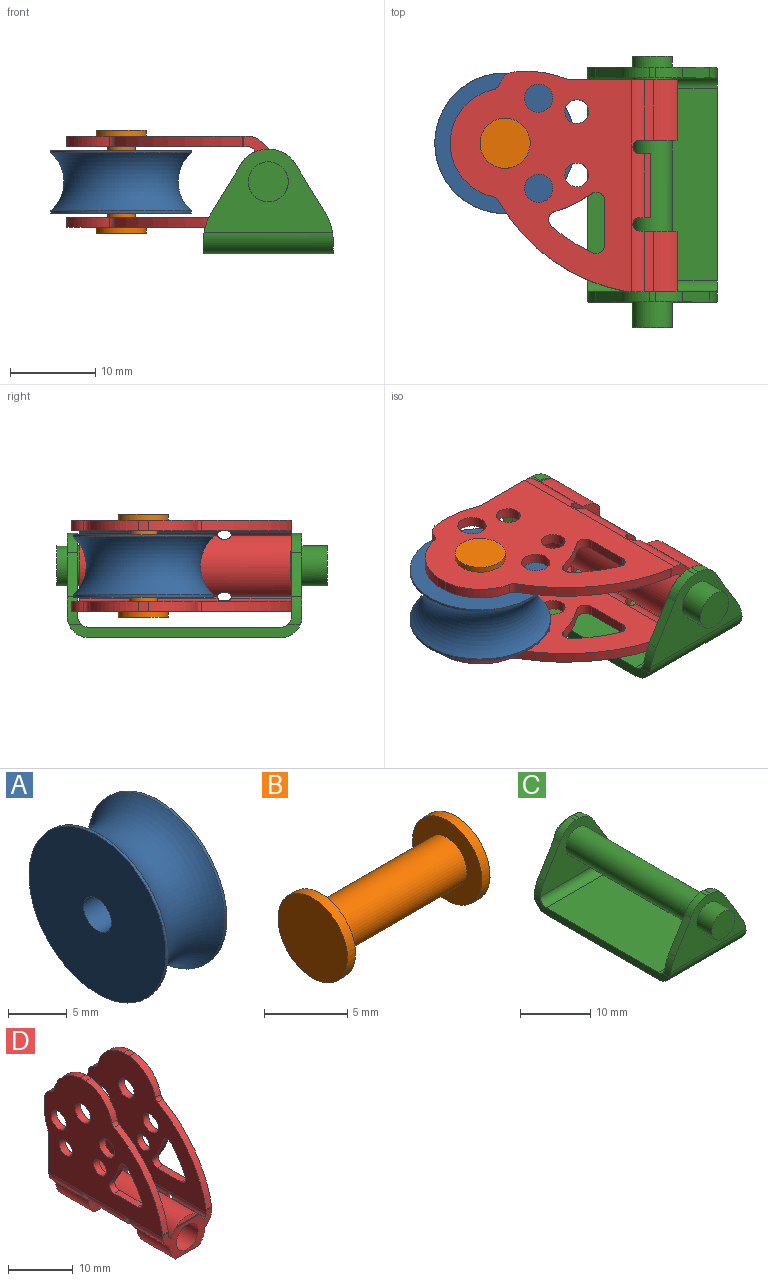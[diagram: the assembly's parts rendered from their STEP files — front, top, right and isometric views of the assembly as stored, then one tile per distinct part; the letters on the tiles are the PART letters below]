
ASSEMBLY  parts=4 mates=3
PART A: 6 faces, bbox 9x24.3x24.3 mm
  f0: cylinder r=8.26mm len=16.51mm, axis (-1,0,0), area 14.2mm2, adj f3,f5
  f1: cylinder r=8.26mm len=16.51mm, axis (-1,0,0), area 14.3mm2, adj f2,f5
  f2: plane 16.51x16.51mm, normal (1,0,0), area 205.3mm2, adj f1,f4
  f3: plane 16.51x16.51mm, normal (-1,0,0), area 205.3mm2, adj f0,f4
  f4: cylinder r=1.68mm len=7.35mm, axis (-1,0,0), area 77.5mm2, adj f2,f3
  f5: torus R=11.22mm, axis (-1,0,0), area 350.3mm2, adj f0,f1
PART B: 7 faces, bbox 12.1x5.9x5.9 mm
  f0: plane 5.89x5.89mm, normal (1,0,0), area 18.4mm2, adj f1,f3
  f1: cylinder r=2.95mm len=5.89mm, axis (1,0,0), area 12.7mm2, adj f0,f2
  f2: plane 5.89x5.89mm, normal (-1,0,0), area 27.3mm2, adj f1
  f3: cylinder r=1.68mm len=10.72mm, axis (1,0,0), area 112.9mm2, adj f0,f6
  f4: plane 5.89x5.89mm, normal (1,0,0), area 27.3mm2, adj f5
  f5: cylinder r=2.95mm len=5.89mm, axis (-1,0,0), area 12.7mm2, adj f4,f6
  f6: plane 5.89x5.89mm, normal (-1,0,0), area 18.4mm2, adj f3,f5
PART C: 31 faces, bbox 15.2x31.9x12.3 mm
  f0: cylinder r=2.35mm len=4.7mm, axis (0,1,0), area 44.2mm2, adj f1,f8
  f1: plane 4.7x4.7mm, normal (0,-1,0), area 17.3mm2, adj f0
  f2: plane 27.18x1.5mm, normal (1,0,0), area 32.2mm2, adj f3,f4,f5,f9,f10,f11,f24,f25
  f3: cylinder r=1.27mm len=15.24mm, axis (-1,0,0), area 30.4mm2, adj f2,f4,f12,f14,f20,f24
  f4: plane 22.61x15.24mm, normal (0,0,1), area 344.5mm2, adj f2,f3,f5,f12
  f5: cylinder r=1.27mm len=15.24mm, axis (-1,0,0), area 30.4mm2, adj f2,f4,f6,f12,f25,f29
  f6: plane 15.09x9.79mm, normal (0,1,0), area 80.7mm2, adj f5,f7,f16,f25,f26,f27,f28,f29
  f7: plane 1.22x0.65mm, normal (0,0,1), area 0.8mm2, adj f6,f8,f27,f30
  f8: plane 15.09x9.79mm, normal (0,-1,0), area 80.7mm2, adj f0,f7,f9,f25,f26,f27,f28,f29
  f9: cylinder r=2.49mm len=15.24mm, axis (-1,0,0), area 59.5mm2, adj f2,f8,f10,f12,f25,f29
  f10: plane 22.61x15.24mm, normal (0,0,-1), area 344.5mm2, adj f2,f9,f11,f12
  f11: cylinder r=2.49mm len=15.24mm, axis (-1,0,0), area 59.5mm2, adj f2,f10,f12,f13,f20,f24
  f12: plane 27.18x1.5mm, normal (-1,0,0), area 32.2mm2, adj f3,f4,f5,f9,f10,f11,f20,f29
  f13: plane 15.09x9.79mm, normal (0,1,0), area 80.7mm2, adj f11,f15,f18,f19,f20,f21,f22,f23
  f14: plane 15.09x9.79mm, normal (0,-1,0), area 80.7mm2, adj f3,f15,f16,f19,f20,f21,f22,f23
  f15: plane 1.22x0.65mm, normal (0,0,1), area 0.8mm2, adj f13,f14,f19,f22
  f16: cylinder r=2.35mm len=25.15mm, axis (0,1,0), area 371.2mm2, adj f6,f14
  f17: plane 4.7x4.7mm, normal (0,1,0), area 17.3mm2, adj f18
  f18: cylinder r=2.35mm len=4.7mm, axis (0,1,0), area 18.7mm2, adj f13,f17
  f19: cylinder r=3.85mm len=3.22mm, axis (0,1,0), area 5.1mm2, adj f13,f14,f15,f21
  f20: cylinder r=6.35mm len=3.32mm, axis (0,1,0), area 4.3mm2, adj f3,f11,f12,f13,f14,f21
  f21: plane 5.13x3.14mm, normal (-0.85,0,0.52), area 7.3mm2, adj f13,f14,f19,f20
  f22: cylinder r=3.85mm len=3.22mm, axis (0,1,0), area 5.1mm2, adj f13,f14,f15,f23
  f23: plane 5.13x3.14mm, normal (0.85,0,0.52), area 7.3mm2, adj f13,f14,f22,f24
  f24: cylinder r=6.35mm len=3.32mm, axis (0,1,0), area 4.3mm2, adj f2,f3,f11,f13,f14,f23
  f25: cylinder r=6.35mm len=3.32mm, axis (0,1,0), area 4.3mm2, adj f2,f5,f6,f8,f9,f26
  f26: plane 5.13x3.14mm, normal (0.85,0,0.52), area 7.3mm2, adj f6,f8,f25,f27
  f27: cylinder r=3.85mm len=3.22mm, axis (0,1,0), area 5.1mm2, adj f6,f7,f8,f26
  f28: plane 5.13x3.14mm, normal (-0.85,0,0.52), area 7.3mm2, adj f6,f8,f29,f30
  f29: cylinder r=6.35mm len=3.32mm, axis (0,1,0), area 4.3mm2, adj f5,f6,f8,f9,f12,f28
  f30: cylinder r=3.85mm len=3.22mm, axis (0,1,0), area 5.1mm2, adj f6,f7,f8,f28
PART D: 96 faces, bbox 10.7x25.9x26.6 mm
  f0: cylinder r=2.35mm len=24.89mm, axis (0,1,0), area 268.2mm2, adj f9,f12,f13,f14,f15,f16,f17,f18
  f1: cylinder r=6.45mm len=5.7mm, axis (-1,0,0), area 9.9mm2, adj f2,f51,f52,f72
  f2: cylinder r=1.02mm len=1.22mm, axis (-1,0,0), area 1.3mm2, adj f1,f3,f51,f52
  f3: cylinder r=2.03mm len=1.69mm, axis (-1,0,0), area 2.8mm2, adj f2,f4,f51,f52
  f4: cylinder r=12.7mm len=6.27mm, axis (-1,0,0), area 7.8mm2, adj f3,f11,f51,f52
  f5: cylinder r=6.45mm len=5.7mm, axis (-1,0,0), area 9.9mm2, adj f6,f41,f68,f73
  f6: cylinder r=1.02mm len=1.22mm, axis (-1,0,0), area 1.3mm2, adj f5,f7,f41,f68
  f7: cylinder r=2.03mm len=1.69mm, axis (-1,0,0), area 2.8mm2, adj f6,f8,f41,f68
  f8: cylinder r=12.7mm len=6.27mm, axis (-1,0,0), area 7.8mm2, adj f7,f10,f41,f68
  f9: plane 12.54x10.72mm, normal (0,1,0), area 48.6mm2, adj f0,f10,f11,f28,f41,f42,f47,f50
  f10: cylinder r=1.02mm len=1.22mm, axis (-1,0,0), area 0.5mm2, adj f8,f9,f41,f68
  f11: cylinder r=1.02mm len=1.22mm, axis (-1,0,0), area 0.5mm2, adj f4,f9,f51,f52
  f12: plane 10.3x4.41mm, normal (0,-1,0), area 18.6mm2, adj f0,f13,f14,f24,f26,f28,f42,f47
  f13: cylinder r=0.79mm len=3mm, axis (-1,0,0), area 5.3mm2, adj f0,f12,f15,f58,f59,f60
  f14: cylinder r=0.79mm len=3mm, axis (-1,0,0), area 5.3mm2, adj f0,f12,f16,f60,f62,f63
  f15: plane 3.33x1.26mm, normal (0,1,0), area 3.2mm2, adj f0,f13,f17,f26,f49,f50,f55,f58
  f16: plane 3.33x1.26mm, normal (0,1,0), area 3.2mm2, adj f0,f14,f18,f24,f42,f44,f62,f65
  f17: plane 7.49x1.81mm, normal (0,0,-1), area 13.6mm2, adj f0,f15,f19,f49
  f18: plane 7.49x1.81mm, normal (0,0,-1), area 13.6mm2, adj f0,f16,f20,f44
  f19: plane 3.33x1.26mm, normal (0,-1,0), area 3.2mm2, adj f0,f17,f21,f27,f49,f50,f55,f58
  f20: plane 3.33x1.26mm, normal (0,-1,0), area 3.2mm2, adj f0,f18,f22,f25,f42,f44,f62,f65
  f21: cylinder r=0.79mm len=3mm, axis (-1,0,0), area 5.3mm2, adj f0,f19,f23,f57,f58,f60
  f22: cylinder r=0.79mm len=3mm, axis (-1,0,0), area 5.3mm2, adj f0,f20,f23,f60,f61,f62
  f23: plane 10.3x4.41mm, normal (0,1,0), area 18.6mm2, adj f0,f21,f22,f25,f27,f40,f42,f43
  f24: cylinder r=0.79mm len=1.71mm, axis (-1,0,0), area 3.2mm2, adj f12,f16,f42,f65,f66,f67
  f25: cylinder r=0.79mm len=1.71mm, axis (-1,0,0), area 3.2mm2, adj f20,f23,f42,f64,f65,f67
  f26: cylinder r=0.79mm len=1.71mm, axis (-1,0,0), area 3.2mm2, adj f12,f15,f50,f53,f55,f56
  f27: cylinder r=0.79mm len=1.71mm, axis (-1,0,0), area 3.2mm2, adj f19,f23,f50,f53,f54,f55
  f28: plane 7.11x5.02mm, normal (0,0,-1), area 35.7mm2, adj f9,f12,f47,f70
  f29: plane 10.72x5.82mm, normal (0,-1,0), area 28.9mm2, adj f0,f30,f34,f36,f40,f41,f42,f43
  f30: cylinder r=1.02mm len=1.22mm, axis (-1,0,0), area 0.2mm2, adj f29,f31,f41,f68
  f31: cylinder r=21.57mm len=14.95mm, axis (-1,0,0), area 23.1mm2, adj f30,f33,f41,f68
  f32: cylinder r=6.45mm len=5.7mm, axis (-1,0,0), area 9.9mm2, adj f33,f41,f68,f73
  f33: cylinder r=1.02mm len=1.22mm, axis (-1,0,0), area 1mm2, adj f31,f32,f41,f68
  f34: cylinder r=1.02mm len=5.06mm, axis (-1,0,0), area 0.9mm2, adj f29,f35,f60
  f35: cylinder r=21.57mm len=4.61mm, axis (-1,0,0), area 2.5mm2, adj f34,f60
  f36: cylinder r=1.02mm len=1.22mm, axis (-1,0,0), area 0.2mm2, adj f29,f37,f51,f52
  f37: cylinder r=21.57mm len=14.95mm, axis (-1,0,0), area 23.1mm2, adj f36,f38,f51,f52
  f38: cylinder r=1.02mm len=1.22mm, axis (-1,0,0), area 1mm2, adj f37,f39,f51,f52
  f39: cylinder r=6.45mm len=5.7mm, axis (-1,0,0), area 9.9mm2, adj f38,f51,f52,f72
  f40: plane 7.11x5.02mm, normal (0,0,-1), area 35.7mm2, adj f23,f29,f45,f46
  f41: plane 25.89x21.29mm, normal (-1,0,0), area 325.9mm2, adj f5,f6,f7,f8,f9,f10,f29,f30
  f42: cylinder r=2.24mm len=24.89mm, axis (0,1,0), area 36.4mm2, adj f9,f12,f16,f20,f23,f24,f25,f29
  f43: plane 7.11x1.06mm, normal (-0.75,0,-0.67), area 10.1mm2, adj f23,f29,f42,f46
  f44: plane 7.49x0.72mm, normal (-0.75,0,-0.67), area 7.2mm2, adj f16,f18,f20,f42
  f45: cylinder r=3.85mm len=7.11mm, axis (0,1,0), area 22.8mm2, adj f23,f29,f40,f48
  f46: cylinder r=3.85mm len=7.11mm, axis (0,1,0), area 22.8mm2, adj f23,f29,f40,f43
  f47: cylinder r=3.85mm len=7.11mm, axis (0,1,0), area 22.8mm2, adj f9,f12,f28,f71
  f48: plane 7.11x1.06mm, normal (0.75,0,-0.67), area 10.1mm2, adj f23,f29,f45,f50
  f49: plane 7.49x0.72mm, normal (0.75,0,-0.67), area 7.2mm2, adj f15,f17,f19,f50
  f50: cylinder r=2.24mm len=24.89mm, axis (0,1,0), area 36.4mm2, adj f9,f12,f15,f19,f23,f26,f27,f29
  f51: plane 25.89x21.29mm, normal (1,0,0), area 325.9mm2, adj f1,f2,f3,f4,f9,f11,f29,f36
  f52: plane 25.89x21.29mm, normal (-1,0,0), area 325.9mm2, adj f1,f2,f3,f4,f9,f11,f29,f36
  f53: cylinder r=1.02mm len=24.89mm, axis (0,1,0), area 17.2mm2, adj f9,f26,f27,f29,f52,f54,f55,f56
  f54: plane 7.16x0.33mm, normal (-0.75,0,0.67), area 3.1mm2, adj f23,f27,f29,f53,f57
  f55: plane 7.59x0.33mm, normal (-0.75,0,0.67), area 3.3mm2, adj f15,f19,f26,f27,f53,f58
  f56: plane 7.16x0.33mm, normal (-0.75,0,0.67), area 3.1mm2, adj f9,f12,f26,f53,f59
  f57: plane 7.11x0.08mm, normal (0.85,0,0.52), area 0.7mm2, adj f21,f23,f29,f54,f60
  f58: plane 7.49x0.08mm, normal (0.85,0,0.52), area 0.7mm2, adj f13,f15,f19,f21,f55,f60
  f59: plane 7.11x0.08mm, normal (0.85,0,0.52), area 0.7mm2, adj f9,f12,f13,f56,f60
  f60: cylinder r=3.85mm len=24.89mm, axis (0,1,0), area 218.9mm2, adj f9,f13,f14,f21,f22,f29,f34,f35
  f61: plane 7.11x0.08mm, normal (-0.85,0,0.52), area 0.7mm2, adj f22,f23,f29,f60,f64
  f62: plane 7.49x0.08mm, normal (-0.85,0,0.52), area 0.7mm2, adj f14,f16,f20,f22,f60,f65
  f63: plane 7.11x0.08mm, normal (-0.85,0,0.52), area 0.7mm2, adj f9,f12,f14,f60,f66
  f64: plane 7.16x0.33mm, normal (0.75,0,0.67), area 3.1mm2, adj f23,f25,f29,f61,f67
  f65: plane 7.59x0.33mm, normal (0.75,0,0.67), area 3.3mm2, adj f16,f20,f24,f25,f62,f67
  f66: plane 7.16x0.33mm, normal (0.75,0,0.67), area 3.1mm2, adj f9,f12,f24,f63,f67
  f67: cylinder r=1.02mm len=24.89mm, axis (0,1,0), area 17.1mm2, adj f9,f24,f25,f29,f64,f65,f66,f68
  f68: plane 25.89x21.29mm, normal (1,0,0), area 325.9mm2, adj f5,f6,f7,f8,f9,f10,f29,f30
  f69: plane 7.11x1.06mm, normal (-0.75,0,-0.67), area 10.1mm2, adj f9,f12,f42,f70
  f70: cylinder r=3.85mm len=7.11mm, axis (0,1,0), area 22.8mm2, adj f9,f12,f28,f69
  f71: plane 7.11x1.06mm, normal (0.75,0,-0.67), area 10.1mm2, adj f9,f12,f47,f50
  f72: plane 1.22x1.19mm, normal (0,0,1), area 1.4mm2, adj f1,f39,f51,f52
  f73: plane 1.22x1.19mm, normal (0,0,1), area 1.4mm2, adj f5,f32,f41,f68
  f74: cylinder r=1.68mm len=3.35mm, axis (-1,0,0), area 12.8mm2, adj f41,f68
  f75: cylinder r=1.4mm len=2.79mm, axis (-1,0,0), area 10.7mm2, adj f41,f68
  f76: cylinder r=1.4mm len=2.79mm, axis (-1,0,0), area 10.7mm2, adj f41,f68
  f77: cylinder r=1.02mm len=1.62mm, axis (-1,0,0), area 2.7mm2, adj f41,f68,f78,f82
  f78: cylinder r=12.7mm len=4.25mm, axis (-1,0,0), area 5.8mm2, adj f41,f68,f77,f79
  f79: cylinder r=1.02mm len=1.74mm, axis (-1,0,0), area 2.7mm2, adj f41,f68,f78,f80
  f80: cylinder r=18.18mm len=4.86mm, axis (-1,0,0), area 7.1mm2, adj f41,f68,f79,f81
  f81: cylinder r=1.02mm len=1.42mm, axis (-1,0,0), area 2.5mm2, adj f41,f68,f80,f82
  f82: plane 5.16x1.22mm, normal (0,0,1), area 6.3mm2, adj f41,f68,f77,f81
  f83: cylinder r=1.66mm len=3.33mm, axis (-1,0,0), area 12.7mm2, adj f41,f68
  f84: cylinder r=1.66mm len=3.33mm, axis (-1,0,0), area 12.7mm2, adj f41,f68
  f85: cylinder r=1.68mm len=3.35mm, axis (-1,0,0), area 12.8mm2, adj f51,f52
  f86: cylinder r=1.4mm len=2.79mm, axis (-1,0,0), area 10.7mm2, adj f51,f52
  f87: cylinder r=1.4mm len=2.79mm, axis (-1,0,0), area 10.7mm2, adj f51,f52
  f88: cylinder r=1.02mm len=1.62mm, axis (-1,0,0), area 2.7mm2, adj f51,f52,f89,f93
  f89: cylinder r=12.7mm len=4.25mm, axis (-1,0,0), area 5.8mm2, adj f51,f52,f88,f90
  f90: cylinder r=1.02mm len=1.74mm, axis (-1,0,0), area 2.7mm2, adj f51,f52,f89,f91
  f91: cylinder r=18.18mm len=4.86mm, axis (-1,0,0), area 7.1mm2, adj f51,f52,f90,f92
  f92: cylinder r=1.02mm len=1.42mm, axis (-1,0,0), area 2.5mm2, adj f51,f52,f91,f93
  f93: plane 5.16x1.22mm, normal (0,0,1), area 6.3mm2, adj f51,f52,f88,f92
  f94: cylinder r=1.66mm len=3.33mm, axis (-1,0,0), area 12.7mm2, adj f51,f52
  f95: cylinder r=1.66mm len=3.33mm, axis (-1,0,0), area 12.7mm2, adj f51,f52
PLACE A rot(axis=(0,-1,0),90deg) t=(0.55,-3.89,-11.32)mm
PLACE B rot(axis=(0,-1,0),90deg) t=(0.55,-3.89,-11.32)mm
PLACE C t=(9.11,-3.63,-2.77)mm
PLACE D rot(axis=(0,-1,0),90deg) t=(0.55,-3.89,-11.32)mm
MATE revolute D.f0 <-> C.f0  axis (0,1,0) through (9.11,-15.34,-11.32)mm
MATE fastened B.f1 <-> D.f1  axis (0,0,1) through (-8.19,2.09,-16.68)mm
MATE revolute A.f0 <-> B.f1  axis (0,0,-1) through (-8.19,2.09,-11.32)mm
